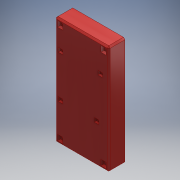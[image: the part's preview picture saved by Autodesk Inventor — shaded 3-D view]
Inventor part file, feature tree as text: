
AUTODESK INVENTOR PART (.ipt)
format: ipt  version: 2017.3 (Build 213256000, 256)  size: 349,184 bytes
history: native  units: mm
features: extrude x11, sketch x10, pattern_linear x1, chamfer x1
ambient origin geometry x8: Origin, YZ Plane, XZ Plane, XY Plane, X Axis, Y Axis, Z Axis, Center Point
bodies: Solid1 (feature_tree)
feature tree (23):
  extrude  "Extrusion1"  Depth=148.0mm
  extrude  "Extrusion2"  Depth=4.0mm
  extrude  "Extrusion4"  TaperAngle=90.0deg  [1 undecoded]
  extrude  "Extrusion10"  Depth=140.0mm
  extrude  "Extrusion11"  Depth=6.0mm
  extrude  "Extrusion12"  Depth=15.0mm TaperAngle=0.0deg
  pattern_linear  "Rectangular Pattern3"  Count1=2 Spacing1=0.0mm
  extrude  "Extrusion13"  Depth=4.0mm
  extrude  "Extrusion14"  Depth=4.0mm
  extrude  "Extrusion15"  Depth=4.0mm
  extrude  "Extrusion17"  Depth=7.75mm
  extrude  "Extrusion18"  Depth=7.2mm
  chamfer  "Chamfer1"  Distance=4.0mm
  sketch  "Sketch1"  dims[d0=73.0mm d1=148.0mm]
  sketch  "Sketch2"  dims[d2=4.0mm d3=0.0mm d4=4.0mm]
  sketch  "Sketch4"  dims[d5=4.0mm d6=90.0deg]
  sketch  "Sketch9"  dims[d7=65.0mm d8=140.0mm]
  sketch  "Sketch10"  dims[d9=18.0mm d10=0.0mm d17=6.0mm]
  sketch  "Sketch11"  dims[d18=6.0mm d19=15.0mm d20=0.0mm]
  sketch  "Sketch12"  dims[d60=7.0mm]
  sketch  "Sketch13"  dims[d61=7.0mm]
  sketch  "Sketch14"  dims[d62=4.1mm d63=20.0mm d64=0.0mm]
  sketch  "Sketch17"  dims[d65=3.6mm d66=3.6mm d67=3.875mm d68=3.875mm d69=7.75mm d70=7.2mm d71=4.0mm d72=0.0mm d73=1.6mm d75=90.0deg d76=1.6mm d77=1.2mm d78=0.0mm d79=20.0mm d81=59.0mm d82=20.0mm d84=134.0mm d85=1.6mm d86=1.6mm d87=90.0deg d88=1.6mm d89=1.6mm d90=90.0deg d91=1.6mm d92=180.0deg d93=1.6mm d94=90.0deg d95=1.2mm d96=0.0mm d97=20.0mm d98=4.0mm d99=61.0mm d100=69.0mm d101=5.5mm d102=52.5mm d103=90.0deg d104=7.0mm d105=3.5mm d106=7.0mm d109=58.0mm d110=7.0mm d111=57.5mm d112=5.5mm d113=7.0mm d114=3.1mm d116=3.1mm d117=3.1mm d118=3.1mm d119=15.0mm d120=0.0mm d121=3.1mm d122=100.0mm d123=0.0mm d124=2.8mm d125=3.1mm d126=5.6mm d127=6.2mm d130=3.1mm d131=2.8mm d132=6.2mm d133=5.6mm d134=2.8mm d135=3.1mm d136=6.2mm d137=5.6mm d138=2.8mm d139=3.1mm d140=6.2mm d141=5.6mm d142=3.0mm d143=0.0mm d144=1.9mm d145=2.1mm d146=2.1mm d147=2.1mm d148=2.1mm d149=4.0mm d150=0.0mm d152=2.0mm d153=2.0mm d154=45.0deg]
note: 1 required parameter value undecoded (feature->parameter linkage not recoverable at this tier; creation-order binding heuristic only, values carry confidence <= 0.55)
